# Revit family: Hand_Shower_Set-DXV-Belshire-D35170780_Series
name_source: partatom
category: Plumbing Fixtures
units: mm (PartAtom-declared; Revit-internal decimal feet)

## family parameters
Cut with Voids When Loaded = No
Host = Face
OmniClass Number = 23.45.05.14.17
OmniClass Title = Showers
Part Type = Normal
Room Calculation Point = No
Round Connector Dimension = Use Radius
Shared = Yes

## types (4) — shared parameters
ASME A112.18.1/CSA B125.1 = Yes
Assembly Code = D2010710
CW Connection = No
CWFU = 3
CalGreen Compliant = Yes
Default Elevation = 48"
Default Elevation Constraint = 48"
Description = Bellshire Personal Hand Shower Set
Flow Rate = 1.8 gpm (6.8 L/min)
HW Connection = No
HWFU = 3
Height = 24"
Installation Type = Wall Mounted
Length = 11 1/32"
Manufacturer = DVX
Price = Prices may vary. Please consult Manufacturer Representative for most up-to-date price list.
Product Documentation Link = https://dxv01.blob.core.windows.net
Product Page URL = https://www.dxv.com
Tempered Water Connection = Yes
Tempered Water Connection Diameter = 1/2"
Tempered Water Connection Radius = 1/4"
URL = http://www.dxv.com
Vent Connection = No
WFU = 4
Waste Connection = No
Width = 2 3/8"

## per-type parameters (varying)
| type | Finish | Material |
| D35170780.100 | Metal-DXV-100-Polished Chrome | Metal-DXV-100-Polished Chrome |
| D35170780.144 | Metal-DXV-144-Brushed Nickel | Metal-DXV-144-Brushed Nickel |
| D35170780.150 | Metal-DXV-150-Platinum Nickel | Metal-DXV-150-Platinum Nickel |
| D35170780.427 | Metal-DXV-427-Satin Brass | Metal-DXV-427-Satin Brass |

note: column(s) folded — value = type name in every type: Model

## geometry (parser evidence)
native form markers: Sweep x2
no freeform markers — native parametric forms only
